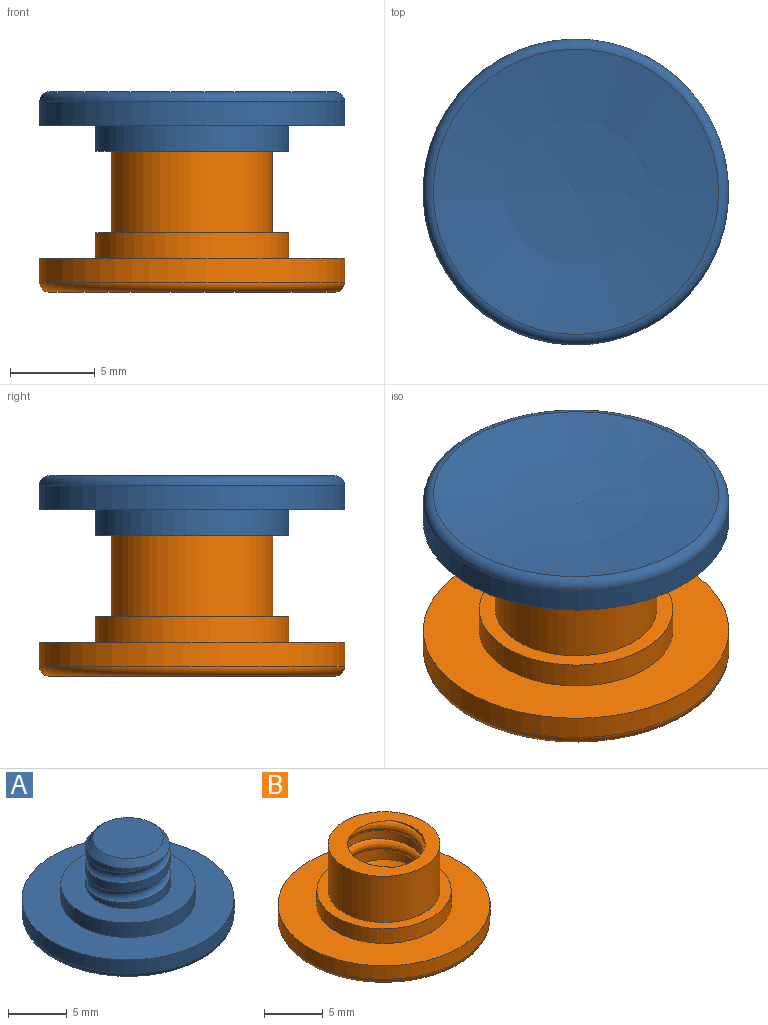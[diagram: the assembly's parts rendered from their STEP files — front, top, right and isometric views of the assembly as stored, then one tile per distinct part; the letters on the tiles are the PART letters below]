
ASSEMBLY  parts=2 mates=1
PART A: 12 faces, bbox 19.6x19.6x9.3 mm
  f0: plane 6x6mm, normal (0,0,1), area 28.3mm2, adj f8
  f1: cylinder r=3.6mm len=7.2mm, axis (0,0,-1), area 47.7mm2, adj f2,f8,f10,f11
  f2: plane 11.4x11.4mm, normal (0,0,1), area 61.4mm2, adj f1,f3,f9
  f3: cylinder r=5.7mm len=11.4mm, axis (0,0,-1), area 53.7mm2, adj f2,f4
  f4: plane 18x18mm, normal (0,0,1), area 152.4mm2, adj f3,f5
  f5: cylinder r=9mm len=18mm, axis (0,0,-1), area 79.2mm2, adj f4,f6
  f6: torus R=8.4mm, axis (0,0,-1), area 52mm2, adj f5,f7
  f7: sphere r=50.75mm, area 223.2mm2, adj f6
  f8: cone r=3.6mm half-angle=45deg, axis (0,0,-1), area 12.6mm2, adj f0,f1,f11
  f9: cylinder r=3.6mm len=0.77mm, axis (0,0,1), area 0mm2, adj f2,f10,f11
  f10: plane 1.21x0.48mm, normal (-1,0,0), area 0.3mm2, adj f1,f9,f11
  f11: bspline ~8.31x7.2mm, area 61.4mm2, adj f1,f8,f9,f10
PART B: 13 faces, bbox 19.8x19.8x9.9 mm
  f0: cylinder r=3.5mm len=7mm, axis (0,0,1), area 40.1mm2, adj f2,f10,f11,f12
  f1: plane 5x5mm, normal (0,0,1), area 19.6mm2, adj f12
  f2: plane 9.83x9.83mm, normal (0,0,1), area 35.9mm2, adj f0,f3,f11
  f3: cylinder r=4.75mm len=9.5mm, axis (0,0,1), area 143.3mm2, adj f2,f4
  f4: plane 11.4x11.4mm, normal (0,0,1), area 31.2mm2, adj f3,f5
  f5: cylinder r=5.7mm len=11.4mm, axis (0,0,1), area 53.7mm2, adj f4,f6
  f6: plane 18x18mm, normal (0,0,1), area 152.4mm2, adj f5,f7
  f7: cylinder r=9mm len=18mm, axis (0,0,1), area 79.2mm2, adj f6,f8
  f8: torus R=8.4mm, axis (0,0,1), area 52mm2, adj f7,f9
  f9: sphere r=50.75mm, area 223.2mm2, adj f8
  f10: plane 0.87x0.5mm, normal (1,0,0), area 0.2mm2, adj f0,f11,f12
  f11: bspline ~8.08x7mm, area 62.2mm2, adj f0,f2,f10,f12
  f12: cone r=2.5mm half-angle=45deg, axis (0,0,1), area 24.7mm2, adj f0,f1,f10,f11
PLACE A rot(axis=(0,1,0),180deg) t=(-30.44,0,11.8)mm
PLACE B at identity
MATE revolute A.f1 <-> B.f8  axis (0,0,-1) through (-30.44,0,8.3)mm
